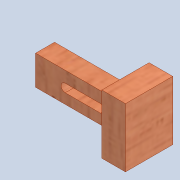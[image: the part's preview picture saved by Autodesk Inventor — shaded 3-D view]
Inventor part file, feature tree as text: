
AUTODESK INVENTOR PART (.ipt)
format: ipt  version: 2020 (Build 240168000, 168)  size: 253,952 bytes
history: native  units: mm
features: extrude x4, sketch x4, fillet x1, mirror x1
ambient origin geometry x8: Origin, YZ Plane, XZ Plane, XY Plane, X Axis, Y Axis, Z Axis, Center Point
bodies: Solid1 (feature_tree)
feature tree (10):
  extrude  "Extrusion1"  Depth=25.0mm
  extrude  "Extrusion5"  Depth=3.5mm
  extrude  "Extrusion6"  Depth=6.0mm
  extrude  "Extrusion7"  Depth=2.0mm
  fillet  "Fillet2"  Radius=15.0mm
  mirror  "Mirror1"
  sketch  "Sketch1"  dims[d0=50.0mm d1=25.0mm]
  sketch  "Sketch5"  dims[d2=20.0mm d3=0.0mm d29=3.5mm]
  sketch  "Sketch6"  dims[d30=4.0mm d31=6.0mm]
  sketch  "Sketch7"  dims[d32=20.0mm d33=15.0mm d34=15.0mm d35=0.0mm d36=10.0mm d37=10.0mm d38=0.0mm d40=12.0mm d41=0.0mm d42=2.0mm]
